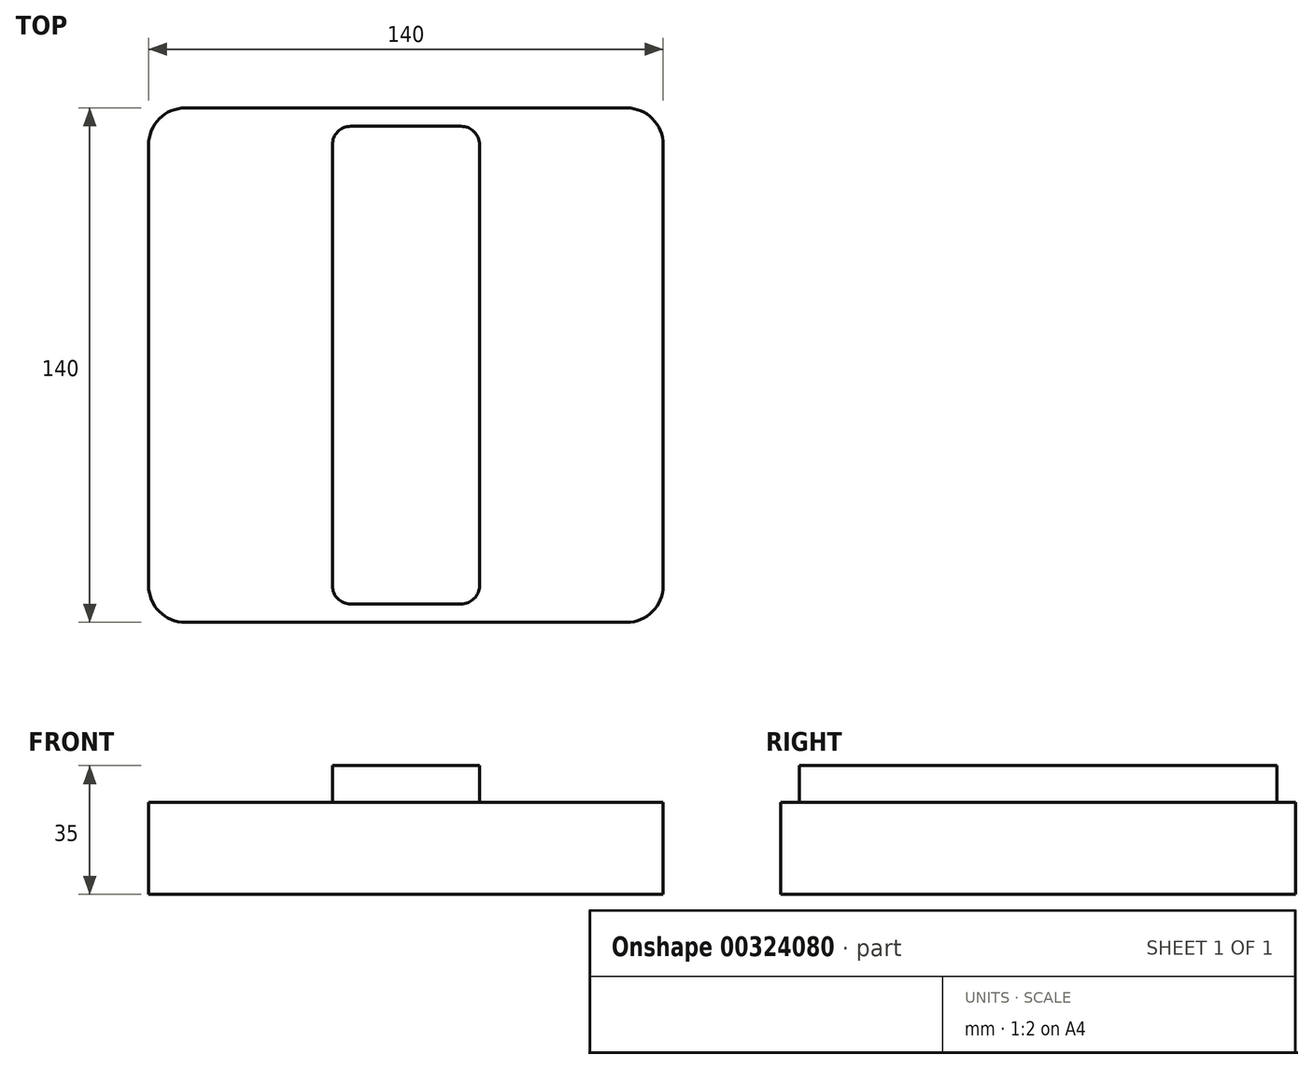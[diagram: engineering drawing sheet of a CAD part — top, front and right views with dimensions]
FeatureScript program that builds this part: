
annotation { "Feature Type Name" : "Feature", "Feature Type Description" : "" }
export const myFeature = defineFeature(function(context is Context, id is Id, definition is map)
    precondition{}
    {
        {
            var Q0;
            Q0=qCreatedBy(makeId("Top.planeOp"),FACE);
            var sketch = newSketch(context, id + "F0", { "sketchPlane" : qUnion([Q0])});
            skLineSegment(sketch, "E0.bottom", {"start": v(70, 70) * mm, "end": v(-70, 70) * mm});
            skLineSegment(sketch, "E0.top", {"start": v(70, -70) * mm, "end": v(-70, -70) * mm});
            skLineSegment(sketch, "E0.left", {"start": v(70, 70) * mm, "end": v(70, -70) * mm});
            skLineSegment(sketch, "E0.right", {"start": v(-70, 70) * mm, "end": v(-70, -70) * mm});
            skPoint(sketch, "E0.middle", {"position": v(0, 0) * mm});
            skLineSegment(sketch, "E1.bottom", {"start": v(-20, 65) * mm, "end": v(20, 65) * mm});
            skLineSegment(sketch, "E1.top", {"start": v(-20, -65) * mm, "end": v(20, -65) * mm});
            skLineSegment(sketch, "E1.left", {"start": v(-20, 65) * mm, "end": v(-20, -65) * mm});
            skLineSegment(sketch, "E1.right", {"start": v(20, 65) * mm, "end": v(20, -65) * mm});
            skSolve(sketch);
        }
        {
            var Q0;
            Q0=makeQuery(id+"F0.imprint","IMPRINT",FACE,{"disambiguationData":[TD([[makeQuery(id+"F0.imprint","IMPRINT",EDGE,{"derivedFrom":sQuery(id+"F0.wireOp",EDGE,"E0.bottom")}),1.0]])]});
            extrude(context, id + "F1", {"entities" : qUnion([Q0]), "depth" : 25 * mm});
        }
        {
            var Q0;
            Q0=makeQuery(id+"F0.imprint","IMPRINT",FACE,{"disambiguationData":[TD([[makeQuery(id+"F0.imprint","IMPRINT",EDGE,{"derivedFrom":sQuery(id+"F0.wireOp",EDGE,"E1.bottom")}),-1.0]])]});
            extrude(context, id + "F2", {"entities" : qUnion([Q0]), "operationType" : NewBodyOperationType.ADD, "depth" : 35 * mm});
        }
        {
            var Q0;
            Q0=makeQuery(id+"F1.opExtrude","SWEPT_EDGE",EDGE,{"disambiguationData":[OSD([sQuery(id+"F0.wireOp",EDGE,"E0.bottom"),sQuery(id+"F0.wireOp",EDGE,"E0.right")])]});
            var Q1;
            Q1=makeQuery(id+"F1.opExtrude","SWEPT_EDGE",EDGE,{"disambiguationData":[OSD([sQuery(id+"F0.wireOp",EDGE,"E0.bottom"),sQuery(id+"F0.wireOp",EDGE,"E0.left")])]});
            var Q2;
            Q2=makeQuery(id+"F1.opExtrude","SWEPT_EDGE",EDGE,{"disambiguationData":[OSD([sQuery(id+"F0.wireOp",EDGE,"E0.top"),sQuery(id+"F0.wireOp",EDGE,"E0.left")])]});
            var Q3;
            Q3=makeQuery(id+"F1.opExtrude","SWEPT_EDGE",EDGE,{"disambiguationData":[OSD([sQuery(id+"F0.wireOp",EDGE,"E0.top"),sQuery(id+"F0.wireOp",EDGE,"E0.right")])]});
            fillet(context, id + "F3", {"entities" : qUnion([Q0, Q1, Q2, Q3]), "radius" : 10 * mm, "tangentPropagation" : true, "allowEdgeOverflow" : false});
        }
        {
            var Q0;
            Q0=makeQuery(id+"F2.opExtrude","SWEPT_EDGE",EDGE,{"disambiguationData":[OSD([sQuery(id+"F0.wireOp",EDGE,"E1.top"),sQuery(id+"F0.wireOp",EDGE,"E1.left")])]});
            var Q1;
            Q1=makeQuery(id+"F2.opExtrude","SWEPT_EDGE",EDGE,{"disambiguationData":[OSD([sQuery(id+"F0.wireOp",EDGE,"E1.top"),sQuery(id+"F0.wireOp",EDGE,"E1.right")])]});
            var Q2;
            Q2=makeQuery(id+"F2.opExtrude","SWEPT_EDGE",EDGE,{"disambiguationData":[OSD([sQuery(id+"F0.wireOp",EDGE,"E1.bottom"),sQuery(id+"F0.wireOp",EDGE,"E1.right")])]});
            var Q3;
            Q3=makeQuery(id+"F2.opExtrude","SWEPT_EDGE",EDGE,{"disambiguationData":[OSD([sQuery(id+"F0.wireOp",EDGE,"E1.bottom"),sQuery(id+"F0.wireOp",EDGE,"E1.left")])]});
            fillet(context, id + "F4", {"entities" : qUnion([Q0, Q1, Q2, Q3]), "radius" : 5 * mm, "tangentPropagation" : true, "allowEdgeOverflow" : false});
        }
    });
